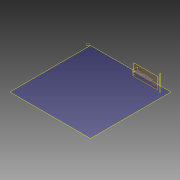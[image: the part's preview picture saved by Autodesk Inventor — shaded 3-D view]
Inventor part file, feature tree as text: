
AUTODESK INVENTOR PART (.ipt)
format: ipt  version: 2012 SP2 (Build 160219200, 219)  size: 491,008 bytes
history: native  units: in
note: dims shown in document units (in); Inventor stores cm internally (conversion verified against a paired STEP export)
features: sketch x10, plane x7, reference x4, sweep x3, extrude x2, helix x1
ambient origin geometry x8: Origin, YZ Plane, XZ Plane, XY Plane, X Axis, Y Axis, Z Axis, Center Point
bodies: Solid1 (feature_tree)
feature tree (27):
  helix  "Coil1"  [1 undecoded]
  sketch  "3D Sketch1"
  plane  "Work Plane1"
  sweep  "Sweep1"
  sweep  "Sweep2"
  plane  "Work Plane2"
  sketch  "Sketch4"  dims[d16=0.1in d17=0.0in]
  sketch  "Sketch5"
  plane  "Work Plane3"
  sweep  "Sweep3"
  plane  "Work Plane4"
  plane  "Work Plane6"
  plane  "Work Plane7"
  extrude  "Extrusion1"  [1 undecoded]
  extrude  "Extrusion2"  [1 undecoded]
  sketch  "Sketch1"  dims[d0=0.1in d1=1.0in d2=11.811in d3=0.0in d4=90.0deg d5=90.0deg d6=0.0in d7=0.0in d8=0.0in]
  sketch  "Sketch2"  dims[d9=0.0in d10=0.0in]
  sketch  "3D Sketch2"
  sketch  "Sketch3"  dims[d11=0.125in d12=0.875in d13=1.0625in d14=0.0in d15=0.0in]
  reference  "Reference1"
  reference  "Reference2"
  reference  "Reference3"
  reference  "Reference4"
  sketch  "Sketch6"
  plane  "Work Plane5"
  sketch  "Sketch9"
  sketch  "Sketch10"
note: 3 required parameter values undecoded (feature->parameter linkage not recoverable at this tier; creation-order binding heuristic only, values carry confidence <= 0.55)
